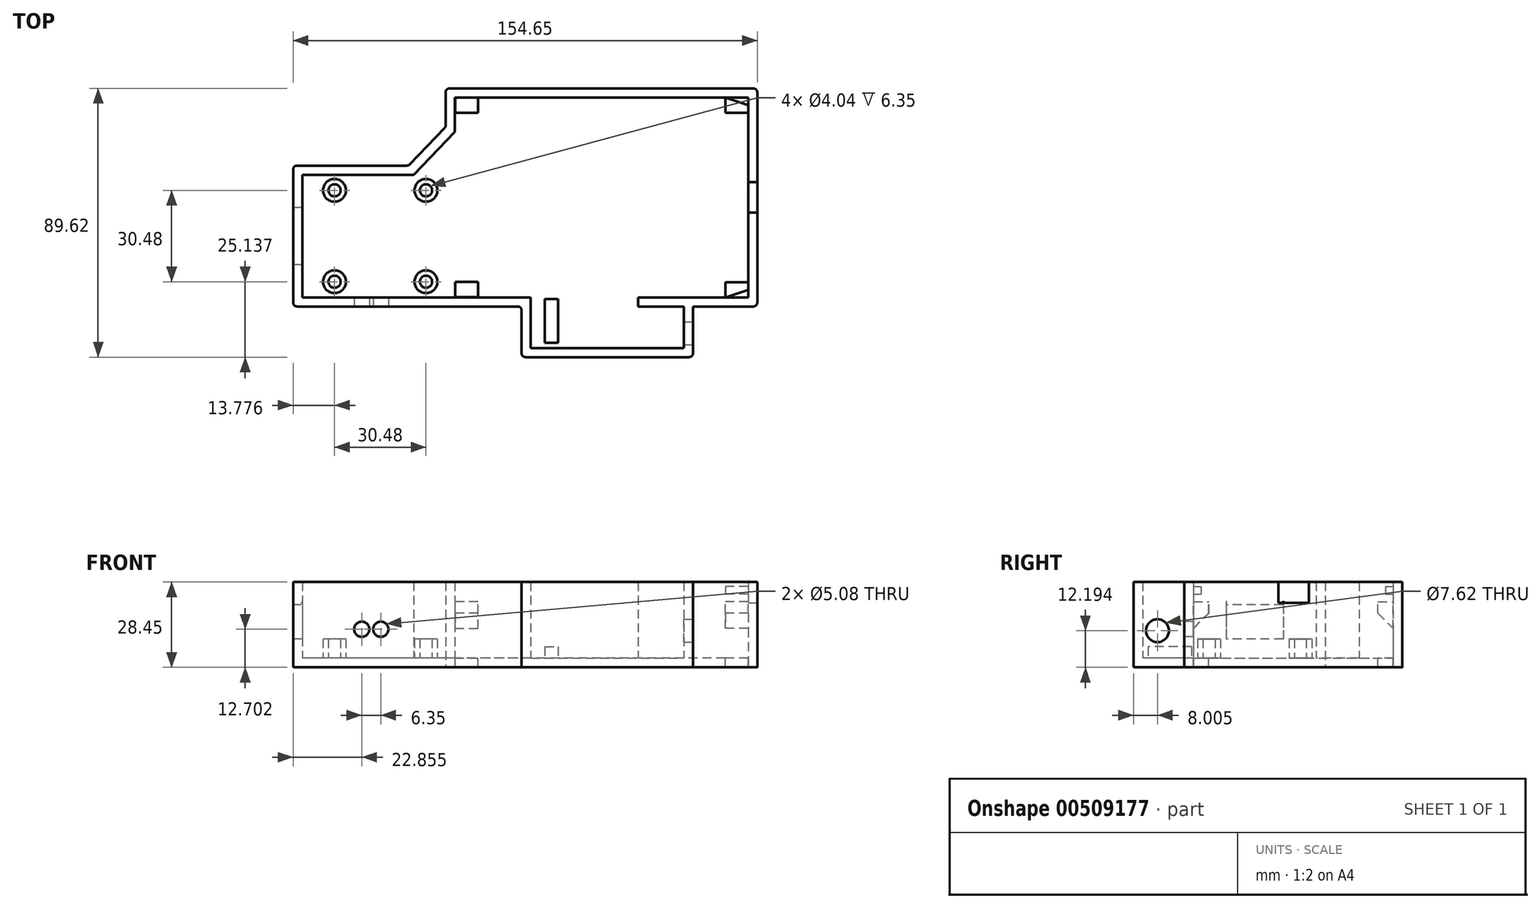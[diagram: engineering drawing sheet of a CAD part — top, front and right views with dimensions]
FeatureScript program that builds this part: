
annotation { "Feature Type Name" : "Feature", "Feature Type Description" : "" }
export const myFeature = defineFeature(function(context is Context, id is Id, definition is map)
    precondition{}
    {
        {
            var Q0;
            Q0=qCreatedBy(makeId("Top.planeOp"),FACE);
            var sketch = newSketch(context, id + "F0", { "sketchPlane" : qUnion([Q0])});
            skPoint(sketch, "E0.middle", {"position": v(0, 0) * mm});
            skLineSegment(sketch, "E1.0", {"start": v(51.92, -36.42) * mm, "end": v(30.54, -36.42) * mm});
            skLineSegment(sketch, "E1.1", {"start": v(51.92, -36.42) * mm, "end": v(51.92, 36.3) * mm});
            skLineSegment(sketch, "E1.2", {"start": v(51.92, 36.3) * mm, "end": v(-51.92, 36.3) * mm});
            skLineSegment(sketch, "E1.3", {"start": v(-51.92, 23.43) * mm, "end": v(-51.92, 36.3) * mm});
            skLineSegment(sketch, "E2.bottom", {"start": v(-51.92, -36.43) * mm, "end": v(-102.73, -36.43) * mm});
            skLineSegment(sketch, "E2.top", {"start": v(-59.67, 10.56) * mm, "end": v(-102.73, 10.56) * mm});
            skLineSegment(sketch, "E2.right", {"start": v(-102.73, -36.43) * mm, "end": v(-102.73, 10.56) * mm});
            skCircle(sketch, "E3", {"center": v(-88.94, -28.18) * mm, "radius": 3.81 * mm});
            skCircle(sketch, "E4", {"center": v(-88.94, -28.18) * mm, "radius": 2.02 * mm});
            skCircle(sketch, "E5.0.1.0", {"center": v(-88.94, 2.3) * mm, "radius": 2.02 * mm});
            skCircle(sketch, "E5.0.1.1", {"center": v(-88.94, 2.3) * mm, "radius": 3.81 * mm});
            skCircle(sketch, "E5.1.0.0", {"center": v(-58.46, -28.18) * mm, "radius": 2.02 * mm});
            skCircle(sketch, "E5.1.0.1", {"center": v(-58.46, -28.18) * mm, "radius": 3.81 * mm});
            skCircle(sketch, "E5.1.1.0", {"center": v(-58.46, 2.3) * mm, "radius": 2.02 * mm});
            skCircle(sketch, "E5.1.1.1", {"center": v(-58.46, 2.3) * mm, "radius": 3.81 * mm});
            skLineSegment(sketch, "E5.direction1", {"start": v(-88.94, -28.18) * mm, "end": v(-58.46, -28.18) * mm, "construction": true});
            skLineSegment(sketch, "E5.direction2", {"start": v(-88.94, -28.18) * mm, "end": v(-88.94, 2.3) * mm, "construction": true});
            skLineSegment(sketch, "E6.top", {"start": v(-26.61, -53.32) * mm, "end": v(30.54, -53.32) * mm});
            skLineSegment(sketch, "E6.left", {"start": v(-26.61, -36.42) * mm, "end": v(-26.61, -53.32) * mm});
            skLineSegment(sketch, "E6.right", {"start": v(30.54, -36.42) * mm, "end": v(30.54, -53.32) * mm});
            skLineSegment(sketch, "E7.trimOffspring", {"start": v(-26.61, -36.42) * mm, "end": v(-51.92, -36.43) * mm});
            skLineSegment(sketch, "E8.0", {"start": v(48.88, 33.25) * mm, "end": v(-48.88, 33.25) * mm});
            skLineSegment(sketch, "E8.1", {"start": v(48.88, -33.38) * mm, "end": v(48.88, 33.25) * mm});
            skLineSegment(sketch, "E8.2", {"start": v(48.88, -33.38) * mm, "end": v(27.49, -33.38) * mm});
            skLineSegment(sketch, "E8.3", {"start": v(27.49, -36.42) * mm, "end": v(27.49, -50.27) * mm});
            skLineSegment(sketch, "E8.4", {"start": v(-23.56, -50.27) * mm, "end": v(27.49, -50.27) * mm});
            skLineSegment(sketch, "E8.5", {"start": v(-48.88, 21.87) * mm, "end": v(-48.88, 33.25) * mm});
            skLineSegment(sketch, "E8.6", {"start": v(-62.58, 7.52) * mm, "end": v(-99.68, 7.52) * mm});
            skLineSegment(sketch, "E8.7", {"start": v(-99.68, -33.38) * mm, "end": v(-99.68, 7.52) * mm});
            skLineSegment(sketch, "E8.8", {"start": v(-51.92, -33.38) * mm, "end": v(-99.68, -33.38) * mm});
            skLineSegment(sketch, "E8.9", {"start": v(-23.56, -33.38) * mm, "end": v(-51.92, -33.38) * mm});
            skLineSegment(sketch, "E8.10", {"start": v(-23.56, -33.38) * mm, "end": v(-23.56, -50.27) * mm});
            skPoint(sketch, "E9.left.start.orphan", {"position": v(-48.75, 33.25) * mm});
            skPoint(sketch, "E10.bottom.start.orphan", {"position": v(48.75, 33.25) * mm});
            skPoint(sketch, "E11.bottom.start.orphan", {"position": v(48.75, -33.25) * mm});
            skPoint(sketch, "E12.bottom.start.orphan", {"position": v(-48.75, -33.25) * mm});
            skLineSegment(sketch, "E13.bottom", {"start": v(48.88, -33.38) * mm, "end": v(41.26, -33.38) * mm});
            skLineSegment(sketch, "E13.top", {"start": v(48.88, -28.3) * mm, "end": v(41.26, -28.3) * mm});
            skLineSegment(sketch, "E13.left", {"start": v(48.88, -33.38) * mm, "end": v(48.88, -28.3) * mm});
            skLineSegment(sketch, "E13.right", {"start": v(41.26, -33.38) * mm, "end": v(41.26, -28.3) * mm});
            skLineSegment(sketch, "E14.bottom", {"start": v(48.88, 33.25) * mm, "end": v(41.26, 33.25) * mm});
            skLineSegment(sketch, "E14.top", {"start": v(48.88, 28.17) * mm, "end": v(41.26, 28.17) * mm});
            skLineSegment(sketch, "E14.left", {"start": v(48.88, 33.25) * mm, "end": v(48.88, 28.17) * mm});
            skLineSegment(sketch, "E14.right", {"start": v(41.26, 33.25) * mm, "end": v(41.26, 28.17) * mm});
            skLineSegment(sketch, "E15.bottom", {"start": v(-48.75, 33.25) * mm, "end": v(-41.13, 33.25) * mm});
            skLineSegment(sketch, "E15.top", {"start": v(-48.75, 28.17) * mm, "end": v(-41.13, 28.17) * mm});
            skLineSegment(sketch, "E15.left", {"start": v(-48.75, 33.25) * mm, "end": v(-48.75, 28.17) * mm});
            skLineSegment(sketch, "E15.right", {"start": v(-41.13, 33.25) * mm, "end": v(-41.13, 28.17) * mm});
            skLineSegment(sketch, "E16.bottom", {"start": v(-48.75, -33.25) * mm, "end": v(-41.13, -33.25) * mm});
            skLineSegment(sketch, "E16.top", {"start": v(-48.75, -28.17) * mm, "end": v(-41.13, -28.17) * mm});
            skLineSegment(sketch, "E16.left", {"start": v(-48.75, -33.25) * mm, "end": v(-48.75, -28.17) * mm});
            skLineSegment(sketch, "E16.right", {"start": v(-41.13, -33.25) * mm, "end": v(-41.13, -28.17) * mm});
            skLineSegment(sketch, "E17.bottom", {"start": v(27.49, -33.38) * mm, "end": v(12.25, -33.38) * mm});
            skLineSegment(sketch, "E17.top", {"start": v(27.49, -36.42) * mm, "end": v(12.25, -36.42) * mm});
            skLineSegment(sketch, "E17.right", {"start": v(12.25, -33.38) * mm, "end": v(12.25, -36.42) * mm});
            skLineSegment(sketch, "E18", {"start": v(-51.92, 23.43) * mm, "end": v(-64.21, 10.56) * mm});
            skLineSegment(sketch, "E19", {"start": v(-59.67, 10.56) * mm, "end": v(-51.92, 18.68) * mm});
            skLineSegment(sketch, "E20", {"start": v(-51.92, 18.68) * mm, "end": v(-48.88, 21.87) * mm});
            skLineSegment(sketch, "E21", {"start": v(-59.67, 10.56) * mm, "end": v(-62.58, 7.52) * mm});
            skPoint(sketch, "E22.orphan", {"position": v(-51.93, 10.56) * mm});
            skSolve(sketch);
        }
        {
            var Q0;
            Q0 = qSketchRegion(id + "F0", true);
            extrude(context, id + "F1", {"entities" : qUnion([Q0]), "depth" : 25.4 * mm});
        }
        {
            var Q0;
            Q0=makeQuery(id+"F0.imprint","IMPRINT",FACE,{"disambiguationData":[TD([[makeQuery(id+"F0.imprint","IMPRINT",EDGE,{"derivedFrom":sQuery(id+"F0.wireOp",EDGE,"E1.0")}),-1.0]])]});
            var Q1;
            Q1=makeQuery(id+"F0.imprint","IMPRINT",FACE,{"disambiguationData":[TD([[makeQuery(id+"F0.imprint","IMPRINT",EDGE,{"derivedFrom":sQuery(id+"F0.wireOp",EDGE,"E3")}),-1.0]])]});
            var Q2;
            Q2=makeQuery(id+"F0.imprint","IMPRINT",FACE,{"disambiguationData":[TD([[makeQuery(id+"F0.imprint","IMPRINT",EDGE,{"derivedFrom":sQuery(id+"F0.wireOp",EDGE,"E5.1.1.0")}),-1.0]])]});
            var Q3;
            Q3=makeQuery(id+"F0.imprint","IMPRINT",FACE,{"disambiguationData":[TD([[makeQuery(id+"F0.imprint","IMPRINT",EDGE,{"derivedFrom":sQuery(id+"F0.wireOp",EDGE,"E5.0.1.0")}),-1.0]])]});
            var Q4;
            Q4=makeQuery(id+"F0.imprint","IMPRINT",FACE,{"disambiguationData":[TD([[makeQuery(id+"F0.imprint","IMPRINT",EDGE,{"derivedFrom":sQuery(id+"F0.wireOp",EDGE,"E5.1.0.0")}),-1.0]])]});
            var Q5;
            Q5=makeQuery(id+"F0.imprint","IMPRINT",FACE,{"disambiguationData":[TD([[makeQuery(id+"F0.imprint","IMPRINT",EDGE,{"derivedFrom":sQuery(id+"F0.wireOp",EDGE,"E4")}),1.0]])]});
            var Q6;
            Q6=makeQuery(id+"F0.imprint","IMPRINT",FACE,{"disambiguationData":[TD([[makeQuery(id+"F0.imprint","IMPRINT",EDGE,{"derivedFrom":sQuery(id+"F0.wireOp",EDGE,"E16.bottom")}),1.0]])]});
            var Q7;
            Q7=makeQuery(id+"F0.imprint","IMPRINT",FACE,{"disambiguationData":[TD([[makeQuery(id+"F0.imprint","IMPRINT",EDGE,{"derivedFrom":sQuery(id+"F0.wireOp",EDGE,"E13.bottom")}),-1.0]])]});
            var Q8;
            Q8=makeQuery(id+"F0.imprint","IMPRINT",FACE,{"disambiguationData":[TD([[makeQuery(id+"F0.imprint","IMPRINT",EDGE,{"derivedFrom":sQuery(id+"F0.wireOp",EDGE,"E14.bottom")}),1.0]])]});
            var Q9;
            Q9=makeQuery(id+"F0.imprint","IMPRINT",FACE,{"disambiguationData":[TD([[makeQuery(id+"F0.imprint","IMPRINT",EDGE,{"derivedFrom":sQuery(id+"F0.wireOp",EDGE,"E15.bottom")}),-1.0]])]});
            var Q10;
            Q10=makeQuery(id+"F0.imprint","IMPRINT",FACE,{"disambiguationData":[TD([[makeQuery(id+"F0.imprint","IMPRINT",EDGE,{"derivedFrom":sQuery(id+"F0.wireOp",EDGE,"E3")}),1.0]])]});
            var Q11;
            Q11=makeQuery(id+"F0.imprint","IMPRINT",FACE,{"disambiguationData":[TD([[makeQuery(id+"F0.imprint","IMPRINT",EDGE,{"derivedFrom":sQuery(id+"F0.wireOp",EDGE,"E5.0.1.0")}),1.0]])]});
            var Q12;
            Q12=makeQuery(id+"F0.imprint","IMPRINT",FACE,{"disambiguationData":[TD([[makeQuery(id+"F0.imprint","IMPRINT",EDGE,{"derivedFrom":sQuery(id+"F0.wireOp",EDGE,"E5.1.1.0")}),1.0]])]});
            var Q13;
            Q13=makeQuery(id+"F0.imprint","IMPRINT",FACE,{"disambiguationData":[TD([[makeQuery(id+"F0.imprint","IMPRINT",EDGE,{"derivedFrom":sQuery(id+"F0.wireOp",EDGE,"E5.1.0.0")}),1.0]])]});
            extrude(context, id + "F2", {"entities" : qUnion([Q0, Q1, Q2, Q3, Q4, Q5, Q6, Q7, Q8, Q9, Q10, Q11, Q12, Q13]), "operationType" : NewBodyOperationType.ADD, "oppositeDirection" : true, "depth" : 3.05 * mm});
        }
        {
            var Q0;
            Q0=makeQuery(id+"F0.imprint","IMPRINT",FACE,{"disambiguationData":[TD([[makeQuery(id+"F0.imprint","IMPRINT",EDGE,{"derivedFrom":sQuery(id+"F0.wireOp",EDGE,"E5.1.1.0")}),-1.0]])]});
            var Q1;
            Q1=makeQuery(id+"F0.imprint","IMPRINT",FACE,{"disambiguationData":[TD([[makeQuery(id+"F0.imprint","IMPRINT",EDGE,{"derivedFrom":sQuery(id+"F0.wireOp",EDGE,"E5.0.1.0")}),-1.0]])]});
            var Q2;
            Q2=makeQuery(id+"F0.imprint","IMPRINT",FACE,{"disambiguationData":[TD([[makeQuery(id+"F0.imprint","IMPRINT",EDGE,{"derivedFrom":sQuery(id+"F0.wireOp",EDGE,"E3")}),1.0]])]});
            var Q3;
            Q3=makeQuery(id+"F0.imprint","IMPRINT",FACE,{"disambiguationData":[TD([[makeQuery(id+"F0.imprint","IMPRINT",EDGE,{"derivedFrom":sQuery(id+"F0.wireOp",EDGE,"E5.1.0.0")}),-1.0]])]});
            extrude(context, id + "F3", {"entities" : qUnion([Q0, Q1, Q2, Q3]), "operationType" : NewBodyOperationType.ADD, "depth" : 6.35 * mm});
        }
        {
            var Q0;
            {var subQ0=sQuery(id+"F0.wireOp",EDGE,"E6.right");Q0=makeQuery(id+"F2.boolean.opBoolean","MERGE",FACE,{"derivedFrom":[makeQuery(id+"F1.opExtrude","SWEPT_FACE",FACE,{"disambiguationData":[OSD([subQ0])]}),makeQuery(id+"F2.opExtrude","SWEPT_FACE",FACE,{"disambiguationData":[OSD([subQ0])]})]});}
            var sketch = newSketch(context, id + "F4", { "sketchPlane" : qUnion([Q0])});
            skCircle(sketch, "E23", {"center": v(-45.31, 9.14) * mm, "radius": 3.81 * mm});
            skSolve(sketch);
        }
        {
            var Q0;
            Q0 = qSketchRegion(id + "F4", true);
            extrude(context, id + "F5", {"entities" : qUnion([Q0]), "operationType" : NewBodyOperationType.REMOVE, "oppositeDirection" : true, "depth" : 6.35 * mm});
        }
        {
            var Q0;
            Q0=makeQuery(id+"F0.imprint","IMPRINT",FACE,{"disambiguationData":[TD([[makeQuery(id+"F0.imprint","IMPRINT",EDGE,{"derivedFrom":sQuery(id+"F0.wireOp",EDGE,"E3")}),-1.0]])]});
            var sketch = newSketch(context, id + "F6", { "sketchPlane" : qUnion([Q0])});
            skLineSegment(sketch, "E24.bottom", {"start": v(-18.86, -34) * mm, "end": v(-14.42, -34) * mm});
            skLineSegment(sketch, "E24.top", {"start": v(-18.86, -48.5) * mm, "end": v(-14.42, -48.5) * mm});
            skLineSegment(sketch, "E24.left", {"start": v(-18.86, -34) * mm, "end": v(-18.86, -48.5) * mm});
            skLineSegment(sketch, "E24.right", {"start": v(-14.42, -34) * mm, "end": v(-14.42, -48.5) * mm});
            skSolve(sketch);
        }
        {
            var Q0;
            Q0 = qSketchRegion(id + "F6", true);
            extrude(context, id + "F7", {"entities" : qUnion([Q0]), "operationType" : NewBodyOperationType.ADD, "depth" : 3.8 * mm});
        }
        {
            var Q0;
            {var subQ0=sQuery(id+"F0.wireOp",EDGE,"E2.right");Q0=makeQuery(id+"F2.boolean.opBoolean","MERGE",FACE,{"derivedFrom":[makeQuery(id+"F1.opExtrude","SWEPT_FACE",FACE,{"disambiguationData":[OSD([subQ0])]}),makeQuery(id+"F2.opExtrude","SWEPT_FACE",FACE,{"disambiguationData":[OSD([subQ0])]})]});}
            var sketch = newSketch(context, id + "F8", { "sketchPlane" : qUnion([Q0])});
            skLineSegment(sketch, "E25.bottom", {"start": v(3.4, 17.78) * mm, "end": v(22.45, 17.78) * mm});
            skLineSegment(sketch, "E25.top", {"start": v(3.4, 6.35) * mm, "end": v(22.45, 6.35) * mm});
            skLineSegment(sketch, "E25.left", {"start": v(3.4, 17.78) * mm, "end": v(3.4, 6.35) * mm});
            skLineSegment(sketch, "E25.right", {"start": v(22.45, 17.78) * mm, "end": v(22.45, 6.35) * mm});
            skSolve(sketch);
        }
        {
            var Q0;
            Q0 = qSketchRegion(id + "F8", true);
            extrude(context, id + "F9", {"entities" : qUnion([Q0]), "operationType" : NewBodyOperationType.REMOVE, "oppositeDirection" : true, "depth" : 5.08 * mm});
        }
        {
            var Q0;
            {var subQ0=sQuery(id+"F0.wireOp",EDGE,"E1.1");Q0=makeQuery(id+"F2.boolean.opBoolean","MERGE",FACE,{"derivedFrom":[makeQuery(id+"F1.opExtrude","SWEPT_FACE",FACE,{"disambiguationData":[OSD([subQ0])]}),makeQuery(id+"F2.opExtrude","SWEPT_FACE",FACE,{"disambiguationData":[OSD([subQ0])]})]});}
            var sketch = newSketch(context, id + "F10", { "sketchPlane" : qUnion([Q0])});
            skLineSegment(sketch, "E26.bottom", {"start": v(5.08, 18.44) * mm, "end": v(-5.08, 18.44) * mm});
            skLineSegment(sketch, "E26.top", {"start": v(5.08, 25.55) * mm, "end": v(-5.08, 25.55) * mm});
            skLineSegment(sketch, "E26.left", {"start": v(5.08, 18.44) * mm, "end": v(5.08, 25.55) * mm});
            skLineSegment(sketch, "E26.right", {"start": v(-5.08, 18.44) * mm, "end": v(-5.08, 25.55) * mm});
            skPoint(sketch, "E26.middle", {"position": v(0, 22) * mm});
            skSolve(sketch);
        }
        {
            var Q0;
            Q0 = qSketchRegion(id + "F10", true);
            extrude(context, id + "F11", {"entities" : qUnion([Q0]), "operationType" : NewBodyOperationType.REMOVE, "oppositeDirection" : true, "depth" : 3.17 * mm});
        }
        {
            var Q0;
            Q0=qCreatedBy(makeId("Top.planeOp"),FACE);
            cPlane(context, id + "F12", {"entities" : qUnion([Q0]), "cplaneType" : CPlaneType.OFFSET, "offset" : 18.8 * mm, "width" : 152.4 * mm, "height" : 152.4 * mm});
        }
        {
            var Q0;
            Q0=qCreatedBy(id+"F12.planeOp",FACE);
            var sketch = newSketch(context, id + "F13", { "sketchPlane" : qUnion([Q0])});
            skLineSegment(sketch, "E27.0.0", {"start": v(-41.13, -28.17) * mm, "end": v(-48.75, -28.17) * mm});
            skLineSegment(sketch, "E27.0.1", {"start": v(-48.75, -28.17) * mm, "end": v(-48.75, -33.25) * mm});
            skLineSegment(sketch, "E27.0.2", {"start": v(-48.75, -33.25) * mm, "end": v(-41.13, -33.25) * mm});
            skLineSegment(sketch, "E27.0.3", {"start": v(-41.13, -33.25) * mm, "end": v(-41.13, -28.17) * mm});
            skLineSegment(sketch, "E28.0.0", {"start": v(41.26, -28.3) * mm, "end": v(41.26, -33.38) * mm});
            skLineSegment(sketch, "E28.0.1", {"start": v(41.26, -33.38) * mm, "end": v(48.88, -33.38) * mm});
            skLineSegment(sketch, "E28.0.2", {"start": v(48.88, -33.38) * mm, "end": v(48.88, -28.3) * mm});
            skLineSegment(sketch, "E28.0.3", {"start": v(48.88, -28.3) * mm, "end": v(41.26, -28.3) * mm});
            skLineSegment(sketch, "E29.0.0", {"start": v(-41.13, 33.25) * mm, "end": v(-48.75, 33.25) * mm});
            skLineSegment(sketch, "E29.0.1", {"start": v(-48.75, 33.25) * mm, "end": v(-48.75, 28.17) * mm});
            skLineSegment(sketch, "E29.0.2", {"start": v(-48.75, 28.17) * mm, "end": v(-41.13, 28.17) * mm});
            skLineSegment(sketch, "E29.0.3", {"start": v(-41.13, 28.17) * mm, "end": v(-41.13, 33.25) * mm});
            skLineSegment(sketch, "E29.1.0", {"start": v(48.88, 28.17) * mm, "end": v(48.88, 33.25) * mm});
            skLineSegment(sketch, "E29.1.1", {"start": v(48.88, 33.25) * mm, "end": v(41.26, 33.25) * mm});
            skLineSegment(sketch, "E29.1.2", {"start": v(41.26, 33.25) * mm, "end": v(41.26, 28.17) * mm});
            skLineSegment(sketch, "E29.1.3", {"start": v(41.26, 28.17) * mm, "end": v(48.88, 28.17) * mm});
            skSolve(sketch);
        }
        {
            var Q0;
            Q0 = qSketchRegion(id + "F13", true);
            extrude(context, id + "F14", {"entities" : qUnion([Q0]), "operationType" : NewBodyOperationType.ADD, "oppositeDirection" : true, "depth" : 12.7 * mm});
        }
        {
            var Q0;
            Q0=makeQuery(id+"F14.opExtrude","CAP_EDGE",EDGE,{"disambiguationData":[OSD([sQuery(id+"F13.wireOp",EDGE,"E29.0.2")])],"isStart":false});
            var Q1;
            Q1=makeQuery(id+"F14.opExtrude","CAP_EDGE",EDGE,{"disambiguationData":[OSD([sQuery(id+"F13.wireOp",EDGE,"E29.1.3")])],"isStart":false});
            var Q2;
            Q2=makeQuery(id+"F14.opExtrude","CAP_EDGE",EDGE,{"disambiguationData":[OSD([sQuery(id+"F13.wireOp",EDGE,"E27.0.0")])],"isStart":false});
            var Q3;
            Q3=makeQuery(id+"F14.opExtrude","CAP_EDGE",EDGE,{"disambiguationData":[OSD([sQuery(id+"F13.wireOp",EDGE,"E28.0.3")])],"isStart":false});
            chamfer(context, id + "F15", {"entities" : qUnion([Q0, Q1, Q2, Q3]), "width" : 8.9 * mm, "tangentPropagation" : true});
        }
        {
            var Q0;
            Q0=qCreatedBy(id+"F12.planeOp",FACE);
            cPlane(context, id + "F16", {"entities" : qUnion([Q0]), "cplaneType" : CPlaneType.OFFSET, "offset" : 2.54 * mm, "width" : 152.4 * mm, "height" : 152.4 * mm});
        }
        {
            var Q0;
            Q0=qCreatedBy(id+"F16.planeOp",FACE);
            var sketch = newSketch(context, id + "F17", { "sketchPlane" : qUnion([Q0])});
            skLineSegment(sketch, "E30.0.0", {"start": v(48.88, -33.38) * mm, "end": v(48.88, -30.84) * mm});
            skLineSegment(sketch, "E30.0.3", {"start": v(41.26, -33.38) * mm, "end": v(48.88, -33.38) * mm});
            skLineSegment(sketch, "E30.1.2", {"start": v(48.88, 28.17) * mm, "end": v(48.88, 33.25) * mm});
            skLineSegment(sketch, "E30.1.3", {"start": v(48.88, 33.25) * mm, "end": v(41.26, 33.25) * mm});
            skLineSegment(sketch, "E31", {"start": v(48.88, -30.84) * mm, "end": v(41.26, -33.38) * mm});
            skPoint(sketch, "E30.0.1.end.orphan", {"position": v(41.26, -28.3) * mm});
            skPoint(sketch, "E32.orphan", {"position": v(48.88, -28.3) * mm});
            skLineSegment(sketch, "E33", {"start": v(48.88, 30.7) * mm, "end": v(41.26, 33.25) * mm});
            skPoint(sketch, "E30.1.1.start.orphan", {"position": v(41.26, 28.17) * mm});
            skSolve(sketch);
        }
        {
            var Q0;
            Q0 = qSketchRegion(id + "F17", true);
            extrude(context, id + "F18", {"entities" : qUnion([Q0]), "operationType" : NewBodyOperationType.ADD, "depth" : 2.54 * mm});
        }
        {
            var Q0;
            {var subQ0=sQuery(id+"F0.wireOp",EDGE,"E7.trimOffspring");var subQ1=sQuery(id+"F0.wireOp",EDGE,"E2.bottom");Q0=makeQuery(id+"F2.boolean.opBoolean","MERGE",FACE,{"derivedFrom":[makeQuery(id+"F1.opExtrude","SWEPT_FACE",FACE,{"disambiguationData":[OSD([subQ1,subQ0])]}),makeQuery(id+"F2.opExtrude","SWEPT_FACE",FACE,{"disambiguationData":[OSD([subQ1,subQ0])]})]});}
            var sketch = newSketch(context, id + "F19", { "sketchPlane" : qUnion([Q0])});
            skCircle(sketch, "E34", {"center": v(-79.87, 9.65) * mm, "radius": 2.54 * mm});
            skCircle(sketch, "E35", {"center": v(-73.52, 9.65) * mm, "radius": 2.54 * mm});
            skSolve(sketch);
        }
        {
            var Q0;
            Q0 = qSketchRegion(id + "F19", true);
            extrude(context, id + "F20", {"entities" : qUnion([Q0]), "operationType" : NewBodyOperationType.REMOVE, "oppositeDirection" : true, "depth" : 3.05 * mm});
        }
        {
            var Q0;
            {var subQ0=sQuery(id+"F0.wireOp",EDGE,"E1.1");var subQ1=sQuery(id+"F0.wireOp",EDGE,"E1.0");Q0=makeQuery(id+"F2.boolean.opBoolean","MERGE",EDGE,{"derivedFrom":[makeQuery(id+"F1.opExtrude","SWEPT_EDGE",EDGE,{"disambiguationData":[OSD([subQ1,subQ0])]}),makeQuery(id+"F2.opExtrude","SWEPT_EDGE",EDGE,{"disambiguationData":[OSD([subQ1,subQ0])]})]});}
            var Q1;
            {var subQ0=sQuery(id+"F0.wireOp",EDGE,"E6.right");var subQ1=sQuery(id+"F0.wireOp",EDGE,"E6.top");Q1=makeQuery(id+"F2.boolean.opBoolean","MERGE",EDGE,{"derivedFrom":[makeQuery(id+"F1.opExtrude","SWEPT_EDGE",EDGE,{"disambiguationData":[OSD([subQ1,subQ0])]}),makeQuery(id+"F2.opExtrude","SWEPT_EDGE",EDGE,{"disambiguationData":[OSD([subQ1,subQ0])]})]});}
            var Q2;
            {var subQ0=sQuery(id+"F0.wireOp",EDGE,"E6.left");var subQ1=sQuery(id+"F0.wireOp",EDGE,"E6.top");Q2=makeQuery(id+"F2.boolean.opBoolean","MERGE",EDGE,{"derivedFrom":[makeQuery(id+"F1.opExtrude","SWEPT_EDGE",EDGE,{"disambiguationData":[OSD([subQ1,subQ0])]}),makeQuery(id+"F2.opExtrude","SWEPT_EDGE",EDGE,{"disambiguationData":[OSD([subQ1,subQ0])]})]});}
            var Q3;
            {var subQ0=sQuery(id+"F0.wireOp",EDGE,"E7.trimOffspring");var subQ1=sQuery(id+"F0.wireOp",EDGE,"E6.left");Q3=makeQuery(id+"F2.boolean.opBoolean","MERGE",EDGE,{"derivedFrom":[makeQuery(id+"F1.opExtrude","SWEPT_EDGE",EDGE,{"disambiguationData":[OSD([subQ1,subQ0])]}),makeQuery(id+"F2.opExtrude","SWEPT_EDGE",EDGE,{"disambiguationData":[OSD([subQ1,subQ0])]})]});}
            var Q4;
            {var subQ0=sQuery(id+"F0.wireOp",EDGE,"E2.right");var subQ1=sQuery(id+"F0.wireOp",EDGE,"E2.bottom");Q4=makeQuery(id+"F2.boolean.opBoolean","MERGE",EDGE,{"derivedFrom":[makeQuery(id+"F1.opExtrude","SWEPT_EDGE",EDGE,{"disambiguationData":[OSD([subQ1,subQ0])]}),makeQuery(id+"F2.opExtrude","SWEPT_EDGE",EDGE,{"disambiguationData":[OSD([subQ1,subQ0])]})]});}
            var Q5;
            {var subQ0=sQuery(id+"F0.wireOp",EDGE,"E2.right");var subQ1=sQuery(id+"F0.wireOp",EDGE,"E2.top");Q5=makeQuery(id+"F2.boolean.opBoolean","MERGE",EDGE,{"derivedFrom":[makeQuery(id+"F1.opExtrude","SWEPT_EDGE",EDGE,{"disambiguationData":[OSD([subQ1,subQ0])]}),makeQuery(id+"F2.opExtrude","SWEPT_EDGE",EDGE,{"disambiguationData":[OSD([subQ1,subQ0])]})]});}
            var Q6;
            {var subQ0=sQuery(id+"F0.wireOp",EDGE,"E18");var subQ1=sQuery(id+"F0.wireOp",EDGE,"E2.top");Q6=makeQuery(id+"F2.boolean.opBoolean","MERGE",EDGE,{"derivedFrom":[makeQuery(id+"F1.opExtrude","SWEPT_EDGE",EDGE,{"disambiguationData":[OSD([subQ1,subQ0])]}),makeQuery(id+"F2.opExtrude","SWEPT_EDGE",EDGE,{"disambiguationData":[OSD([subQ1,subQ0])]})]});}
            var Q7;
            {var subQ0=sQuery(id+"F0.wireOp",EDGE,"E18");var subQ1=sQuery(id+"F0.wireOp",EDGE,"E1.3");Q7=makeQuery(id+"F2.boolean.opBoolean","MERGE",EDGE,{"derivedFrom":[makeQuery(id+"F1.opExtrude","SWEPT_EDGE",EDGE,{"disambiguationData":[OSD([subQ1,subQ0])]}),makeQuery(id+"F2.opExtrude","SWEPT_EDGE",EDGE,{"disambiguationData":[OSD([subQ1,subQ0])]})]});}
            var Q8;
            {var subQ0=sQuery(id+"F0.wireOp",EDGE,"E1.3");var subQ1=sQuery(id+"F0.wireOp",EDGE,"E1.2");Q8=makeQuery(id+"F2.boolean.opBoolean","MERGE",EDGE,{"derivedFrom":[makeQuery(id+"F1.opExtrude","SWEPT_EDGE",EDGE,{"disambiguationData":[OSD([subQ1,subQ0])]}),makeQuery(id+"F2.opExtrude","SWEPT_EDGE",EDGE,{"disambiguationData":[OSD([subQ1,subQ0])]})]});}
            var Q9;
            {var subQ0=sQuery(id+"F0.wireOp",EDGE,"E1.2");var subQ1=sQuery(id+"F0.wireOp",EDGE,"E1.1");Q9=makeQuery(id+"F2.boolean.opBoolean","MERGE",EDGE,{"derivedFrom":[makeQuery(id+"F1.opExtrude","SWEPT_EDGE",EDGE,{"disambiguationData":[OSD([subQ1,subQ0])]}),makeQuery(id+"F2.opExtrude","SWEPT_EDGE",EDGE,{"disambiguationData":[OSD([subQ1,subQ0])]})]});}
            var Q10;
            Q10=makeQuery(id+"F3.opExtrude","CAP_EDGE",EDGE,{"disambiguationData":[OSD([sQuery(id+"F0.wireOp",EDGE,"E5.1.0.1")])],"isStart":true});
            var Q11;
            Q11=makeQuery(id+"F3.opExtrude","CAP_EDGE",EDGE,{"disambiguationData":[OSD([sQuery(id+"F0.wireOp",EDGE,"E3")])],"isStart":true});
            var Q12;
            Q12=makeQuery(id+"F3.opExtrude","CAP_EDGE",EDGE,{"disambiguationData":[OSD([sQuery(id+"F0.wireOp",EDGE,"E5.1.1.1")])],"isStart":true});
            var Q13;
            Q13=makeQuery(id+"F3.opExtrude","CAP_EDGE",EDGE,{"disambiguationData":[OSD([sQuery(id+"F0.wireOp",EDGE,"E5.0.1.1")])],"isStart":true});
            var Q14;
            Q14=makeQuery(id+"F11.boolean.opBoolean","COPY",EDGE,{"derivedFrom":makeQuery(id+"F11.opExtrude","CAP_EDGE",EDGE,{"disambiguationData":[OSD([sQuery(id+"F10.wireOp",EDGE,"E26.right")])],"isStart":true})});
            var Q15;
            Q15=makeQuery(id+"F11.boolean.opBoolean","COPY",EDGE,{"derivedFrom":makeQuery(id+"F11.opExtrude","CAP_EDGE",EDGE,{"disambiguationData":[OSD([sQuery(id+"F10.wireOp",EDGE,"E26.bottom")])],"isStart":true})});
            var Q16;
            Q16=makeQuery(id+"F11.boolean.opBoolean","COPY",EDGE,{"derivedFrom":makeQuery(id+"F11.opExtrude","CAP_EDGE",EDGE,{"disambiguationData":[OSD([sQuery(id+"F10.wireOp",EDGE,"E26.left")])],"isStart":true})});
            var Q17;
            Q17=makeQuery(id+"F9.boolean.opBoolean","INTERSECT",EDGE,{"derivedFrom":[makeQuery(id+"F1.opExtrude","SWEPT_FACE",FACE,{"disambiguationData":[OSD([sQuery(id+"F0.wireOp",EDGE,"E8.7")])]}),makeQuery(id+"F9.opExtrude","SWEPT_FACE",FACE,{"disambiguationData":[OSD([sQuery(id+"F8.wireOp",EDGE,"E25.bottom")])]})]});
            fillet(context, id + "F21", {"entities" : qUnion([Q0, Q1, Q2, Q3, Q4, Q5, Q6, Q7, Q8, Q9, Q10, Q11, Q12, Q13, Q14, Q15, Q16, Q17]), "radius" : 1.27 * mm, "tangentPropagation" : true, "allowEdgeOverflow" : false});
        }
    });
